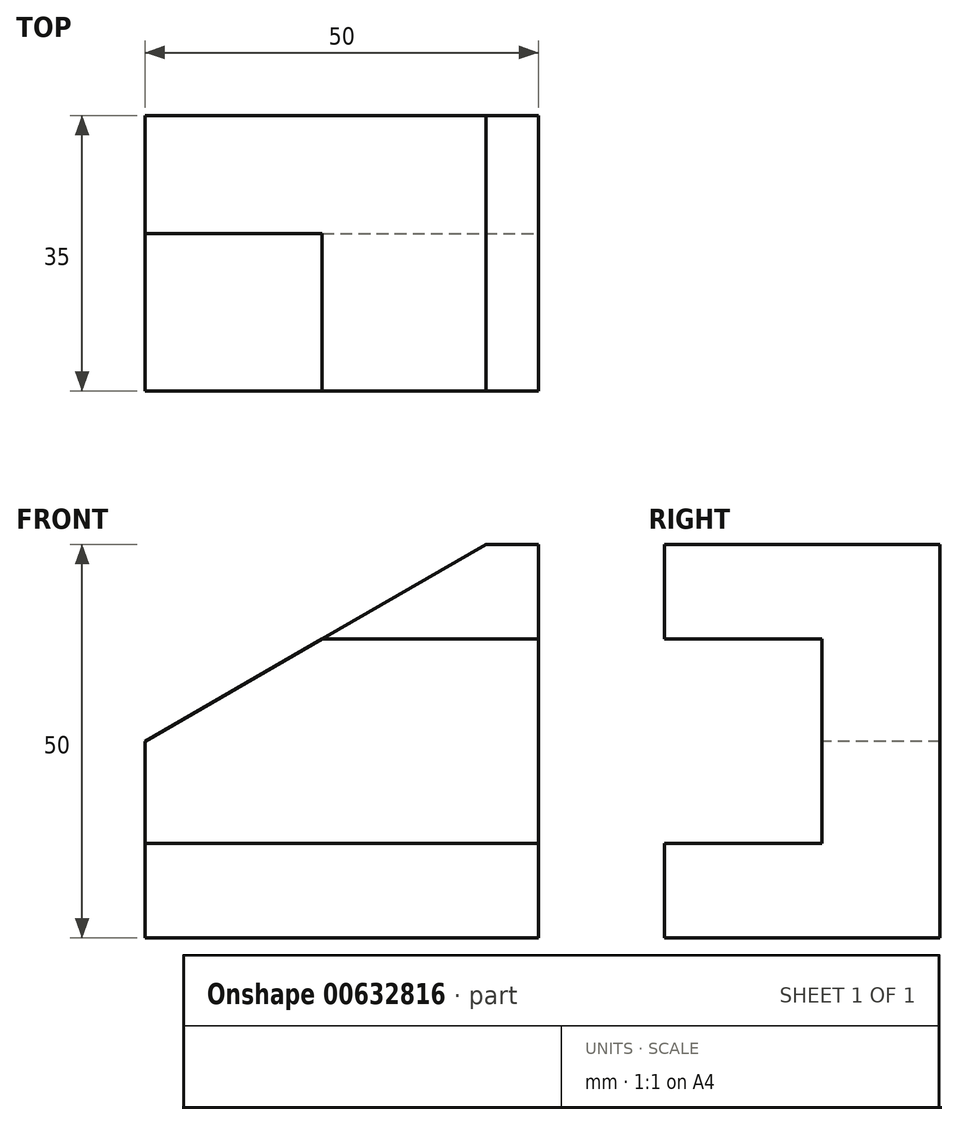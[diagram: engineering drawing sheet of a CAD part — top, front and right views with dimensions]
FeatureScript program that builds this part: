
annotation { "Feature Type Name" : "Feature", "Feature Type Description" : "" }
export const myFeature = defineFeature(function(context is Context, id is Id, definition is map)
    precondition{}
    {
        {
            var Q0;
            Q0=qCreatedBy(makeId("Front.planeOp"),FACE);
            var sketch = newSketch(context, id + "F0", { "sketchPlane" : qUnion([Q0])});
            skLineSegment(sketch, "E0.bottom", {"start": v(-25, 25) * mm, "end": v(25, 25) * mm});
            skLineSegment(sketch, "E0.top", {"start": v(-25, -25) * mm, "end": v(25, -25) * mm});
            skLineSegment(sketch, "E0.left", {"start": v(-25, 25) * mm, "end": v(-25, -25) * mm});
            skLineSegment(sketch, "E0.right", {"start": v(25, 25) * mm, "end": v(25, -25) * mm});
            skPoint(sketch, "E0.middle", {"position": v(0, 0) * mm});
            skSolve(sketch);
        }
        {
            var Q0;
            Q0 = qSketchRegion(id + "F0", true);
            extrude(context, id + "F1", {"entities" : qUnion([Q0]), "depth" : 35 * mm, "offsetDistance" : 25 * mm});
        }
        {
            var Q0;
            Q0=makeQuery(id+"F1.opExtrude","CAP_FACE",FACE,{"disambiguationData":[OSD([sQuery(id+"F0.wireOp",EDGE,"E0.bottom"),sQuery(id+"F0.wireOp",EDGE,"E0.top"),sQuery(id+"F0.wireOp",EDGE,"E0.left"),sQuery(id+"F0.wireOp",EDGE,"E0.right")])],"isStart":false});
            var sketch = newSketch(context, id + "F2", { "sketchPlane" : qUnion([Q0])});
            skLineSegment(sketch, "E1", {"start": v(18.3, 25) * mm, "end": v(-25, 0) * mm});
            skSolve(sketch);
        }
        {
            var Q0;
            Q0 = qSketchRegion(id + "F2", true);
            var Q1;
            {var subQ0=sQuery(id+"F2.wireOp",EDGE,"E1");Q1=makeQuery(id+"F2.imprint","IMPRINT",FACE,{"disambiguationData":[TD([[makeQuery(id+"F2.imprint","IMPRINT",EDGE,{"derivedFrom":subQ0}),-1.0]])]});}
            extrude(context, id + "F3", {"entities" : qUnion([Q0, Q1]), "operationType" : NewBodyOperationType.REMOVE, "endBound" : BoundingType.THROUGH_ALL, "oppositeDirection" : true, "depth" : 25 * mm, "offsetDistance" : 25 * mm});
        }
        {
            var Q0;
            Q0=makeQuery(id+"F1.opExtrude","CAP_FACE",FACE,{"disambiguationData":[OSD([sQuery(id+"F0.wireOp",EDGE,"E0.bottom"),sQuery(id+"F0.wireOp",EDGE,"E0.top"),sQuery(id+"F0.wireOp",EDGE,"E0.left"),sQuery(id+"F0.wireOp",EDGE,"E0.right")])],"isStart":false});
            var sketch = newSketch(context, id + "F4", { "sketchPlane" : qUnion([Q0])});
            skLineSegment(sketch, "E2", {"start": v(-25, -13) * mm, "end": v(25, -13) * mm});
            skLineSegment(sketch, "E3", {"start": v(-2.48, 13) * mm, "end": v(25, 13) * mm});
            skSolve(sketch);
        }
        {
            var Q0;
            {var subQ4=sQuery(id+"F4.wireOp",EDGE,"E2");Q0=makeQuery(id+"F4.imprint","IMPRINT",FACE,{"disambiguationData":[TD([[makeQuery(id+"F4.imprint","IMPRINT",EDGE,{"derivedFrom":subQ4}),1.0]])]});}
            extrude(context, id + "F5", {"entities" : qUnion([Q0]), "operationType" : NewBodyOperationType.REMOVE, "oppositeDirection" : true, "depth" : 20 * mm, "offsetDistance" : 25 * mm});
        }
    });
